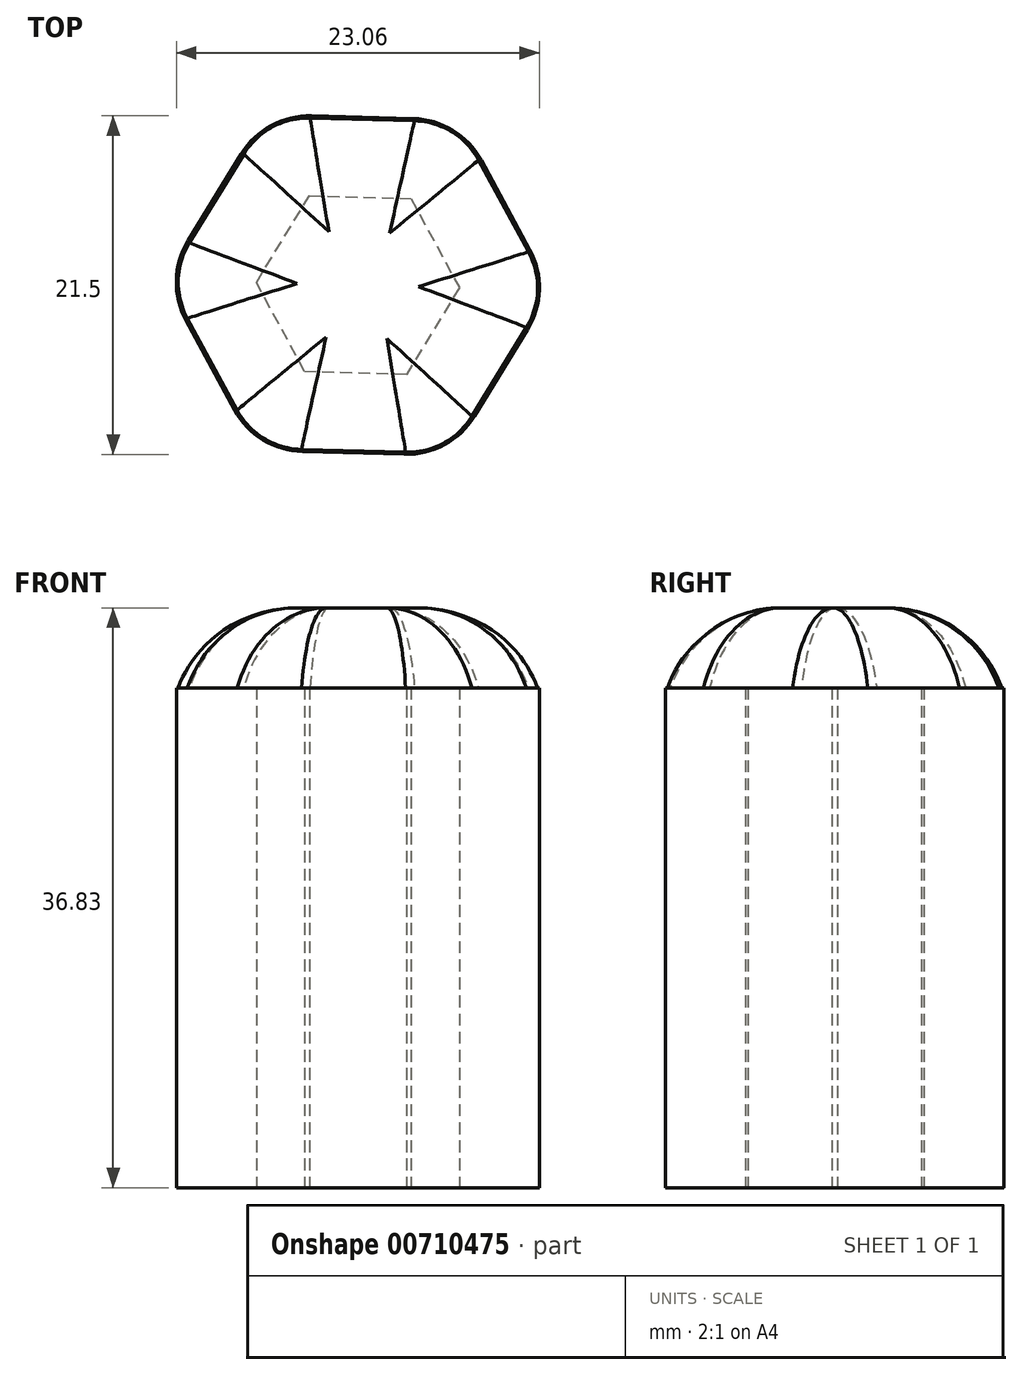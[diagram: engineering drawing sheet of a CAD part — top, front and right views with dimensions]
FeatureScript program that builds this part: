
annotation { "Feature Type Name" : "Feature", "Feature Type Description" : "" }
export const myFeature = defineFeature(function(context is Context, id is Id, definition is map)
    precondition{}
    {
        {
            var Q0;
            Q0=qCreatedBy(makeId("Top.planeOp"),FACE);
            var sketch = newSketch(context, id + "F0", { "sketchPlane" : qUnion([Q0])});
            skCircle(sketch, "E0.cCircle", {"center": v(0, 0) * mm, "radius": 5.59 * mm, "construction": true});
            skLineSegment(sketch, "E0.0", {"start": v(6.45, -0.17) * mm, "end": v(3.08, -5.67) * mm});
            skLineSegment(sketch, "E0.1", {"start": v(3.08, -5.67) * mm, "end": v(-3.37, -5.5) * mm});
            skLineSegment(sketch, "E0.2", {"start": v(-3.37, -5.5) * mm, "end": v(-6.45, 0.17) * mm});
            skLineSegment(sketch, "E0.3", {"start": v(-6.45, 0.17) * mm, "end": v(-3.08, 5.67) * mm});
            skLineSegment(sketch, "E0.4", {"start": v(-3.08, 5.67) * mm, "end": v(3.37, 5.5) * mm});
            skLineSegment(sketch, "E0.5", {"start": v(3.37, 5.5) * mm, "end": v(6.45, -0.17) * mm});
            skPoint(sketch, "E0.0.midPoint", {"position": v(4.76, -2.92) * mm});
            skCircle(sketch, "E1.cCircle", {"center": v(0, 0) * mm, "radius": 10.67 * mm, "construction": true});
            skLineSegment(sketch, "E1.0", {"start": v(12.31, -0.32) * mm, "end": v(5.88, -10.83) * mm});
            skLineSegment(sketch, "E1.1", {"start": v(5.88, -10.83) * mm, "end": v(-6.44, -10.5) * mm});
            skLineSegment(sketch, "E1.2", {"start": v(-6.44, -10.5) * mm, "end": v(-12.31, 0.32) * mm});
            skLineSegment(sketch, "E1.3", {"start": v(-12.31, 0.32) * mm, "end": v(-5.88, 10.83) * mm});
            skLineSegment(sketch, "E1.4", {"start": v(-5.88, 10.83) * mm, "end": v(6.44, 10.5) * mm});
            skLineSegment(sketch, "E1.5", {"start": v(6.44, 10.5) * mm, "end": v(12.31, -0.32) * mm});
            skPoint(sketch, "E1.0.midPoint", {"position": v(9.1, -5.57) * mm});
            skSolve(sketch);
        }
        {
            var Q0;
            Q0 = qSketchRegion(id + "F0", true);
            extrude(context, id + "F1", {"entities" : qUnion([Q0]), "depth" : 31.75 * mm, "offsetDistance" : 25.4 * mm});
        }
        {
            var Q0;
            Q0=makeQuery(id+"F1.opExtrude","CAP_FACE",FACE,{"disambiguationData":[OSD([sQuery(id+"F0.wireOp",EDGE,"E0.0"),sQuery(id+"F0.wireOp",EDGE,"E0.1"),sQuery(id+"F0.wireOp",EDGE,"E0.2"),sQuery(id+"F0.wireOp",EDGE,"E0.3"),sQuery(id+"F0.wireOp",EDGE,"E0.4"),sQuery(id+"F0.wireOp",EDGE,"E0.5"),sQuery(id+"F0.wireOp",EDGE,"E1.0"),sQuery(id+"F0.wireOp",EDGE,"E1.1"),sQuery(id+"F0.wireOp",EDGE,"E1.2"),sQuery(id+"F0.wireOp",EDGE,"E1.3"),sQuery(id+"F0.wireOp",EDGE,"E1.4"),sQuery(id+"F0.wireOp",EDGE,"E1.5")])],"isStart":false});
            var sketch = newSketch(context, id + "F2", { "sketchPlane" : qUnion([Q0])});
            skCircle(sketch, "E2.cCircle", {"center": v(0, 0) * mm, "radius": 10.53 * mm, "construction": true});
            skLineSegment(sketch, "E2.0", {"start": v(12.15, -0.32) * mm, "end": v(5.8, -10.68) * mm});
            skLineSegment(sketch, "E2.1", {"start": v(5.8, -10.68) * mm, "end": v(-6.35, -10.36) * mm});
            skLineSegment(sketch, "E2.2", {"start": v(-6.35, -10.36) * mm, "end": v(-12.15, 0.32) * mm});
            skLineSegment(sketch, "E2.3", {"start": v(-12.15, 0.32) * mm, "end": v(-5.8, 10.68) * mm});
            skLineSegment(sketch, "E2.4", {"start": v(-5.8, 10.68) * mm, "end": v(6.35, 10.36) * mm});
            skLineSegment(sketch, "E2.5", {"start": v(6.35, 10.36) * mm, "end": v(12.15, -0.32) * mm});
            skPoint(sketch, "E2.0.midPoint", {"position": v(8.98, -5.5) * mm});
            skSolve(sketch);
        }
        {
            var Q0;
            Q0 = qSketchRegion(id + "F2", true);
            extrude(context, id + "F3", {"entities" : qUnion([Q0]), "operationType" : NewBodyOperationType.ADD, "depth" : 5.08 * mm, "offsetDistance" : 25.4 * mm});
        }
        {
            var Q0;
            Q0=makeQuery(id+"F3.opExtrude","CAP_EDGE",EDGE,{"disambiguationData":[OSD([sQuery(id+"F2.wireOp",EDGE,"E2.1")])],"isStart":false});
            var Q1;
            Q1=makeQuery(id+"F3.opExtrude","CAP_EDGE",EDGE,{"disambiguationData":[OSD([sQuery(id+"F2.wireOp",EDGE,"E2.0")])],"isStart":false});
            var Q2;
            Q2=makeQuery(id+"F3.opExtrude","CAP_EDGE",EDGE,{"disambiguationData":[OSD([sQuery(id+"F2.wireOp",EDGE,"E2.2")])],"isStart":false});
            var Q3;
            Q3=makeQuery(id+"F3.opExtrude","CAP_EDGE",EDGE,{"disambiguationData":[OSD([sQuery(id+"F2.wireOp",EDGE,"E2.3")])],"isStart":false});
            var Q4;
            Q4=makeQuery(id+"F3.opExtrude","CAP_EDGE",EDGE,{"disambiguationData":[OSD([sQuery(id+"F2.wireOp",EDGE,"E2.4")])],"isStart":false});
            var Q5;
            Q5=makeQuery(id+"F3.opExtrude","CAP_EDGE",EDGE,{"disambiguationData":[OSD([sQuery(id+"F2.wireOp",EDGE,"E2.5")])],"isStart":false});
            fillet(context, id + "F4", {"entities" : qUnion([Q0, Q1, Q2, Q3, Q4, Q5]), "radius" : 7.62 * mm, "tangentPropagation" : true, "allowEdgeOverflow" : false});
        }
        {
            var Q0;
            Q0=makeQuery(id+"F4.opFillet","BLEND_EDGE",EDGE,{"blendedFrom":[makeQuery(id+"F3.opExtrude","CAP_EDGE",EDGE,{"disambiguationData":[OSD([sQuery(id+"F2.wireOp",EDGE,"E2.0")])],"isStart":false}),makeQuery(id+"F3.opExtrude","CAP_EDGE",EDGE,{"disambiguationData":[OSD([sQuery(id+"F2.wireOp",EDGE,"E2.5")])],"isStart":false})],"blendedInto":[]});
            var Q1;
            Q1=makeQuery(id+"F1.opExtrude","SWEPT_EDGE",EDGE,{"disambiguationData":[OSD([sQuery(id+"F0.wireOp",EDGE,"E1.4"),sQuery(id+"F0.wireOp",EDGE,"E1.5")])]});
            var Q2;
            Q2=makeQuery(id+"F1.opExtrude","SWEPT_EDGE",EDGE,{"disambiguationData":[OSD([sQuery(id+"F0.wireOp",EDGE,"E1.0"),sQuery(id+"F0.wireOp",EDGE,"E1.5")])]});
            var Q3;
            Q3=makeQuery(id+"F4.opFillet","BLEND_EDGE",EDGE,{"blendedFrom":[makeQuery(id+"F3.opExtrude","CAP_EDGE",EDGE,{"disambiguationData":[OSD([sQuery(id+"F2.wireOp",EDGE,"E2.4")])],"isStart":false}),makeQuery(id+"F3.opExtrude","CAP_EDGE",EDGE,{"disambiguationData":[OSD([sQuery(id+"F2.wireOp",EDGE,"E2.5")])],"isStart":false})],"blendedInto":[]});
            var Q4;
            Q4=makeQuery(id+"F4.opFillet","BLEND_EDGE",EDGE,{"blendedFrom":[makeQuery(id+"F3.opExtrude","CAP_EDGE",EDGE,{"disambiguationData":[OSD([sQuery(id+"F2.wireOp",EDGE,"E2.3")])],"isStart":false}),makeQuery(id+"F3.opExtrude","CAP_EDGE",EDGE,{"disambiguationData":[OSD([sQuery(id+"F2.wireOp",EDGE,"E2.4")])],"isStart":false})],"blendedInto":[]});
            var Q5;
            Q5=makeQuery(id+"F4.opFillet","BLEND_EDGE",EDGE,{"blendedFrom":[makeQuery(id+"F3.opExtrude","CAP_EDGE",EDGE,{"disambiguationData":[OSD([sQuery(id+"F2.wireOp",EDGE,"E2.0")])],"isStart":false}),makeQuery(id+"F3.opExtrude","CAP_EDGE",EDGE,{"disambiguationData":[OSD([sQuery(id+"F2.wireOp",EDGE,"E2.1")])],"isStart":false})],"blendedInto":[]});
            var Q6;
            Q6=makeQuery(id+"F4.opFillet","BLEND_EDGE",EDGE,{"blendedFrom":[makeQuery(id+"F3.opExtrude","CAP_EDGE",EDGE,{"disambiguationData":[OSD([sQuery(id+"F2.wireOp",EDGE,"E2.1")])],"isStart":false}),makeQuery(id+"F3.opExtrude","CAP_EDGE",EDGE,{"disambiguationData":[OSD([sQuery(id+"F2.wireOp",EDGE,"E2.2")])],"isStart":false})],"blendedInto":[]});
            var Q7;
            Q7=makeQuery(id+"F4.opFillet","BLEND_EDGE",EDGE,{"blendedFrom":[makeQuery(id+"F3.opExtrude","CAP_EDGE",EDGE,{"disambiguationData":[OSD([sQuery(id+"F2.wireOp",EDGE,"E2.2")])],"isStart":false}),makeQuery(id+"F3.opExtrude","CAP_EDGE",EDGE,{"disambiguationData":[OSD([sQuery(id+"F2.wireOp",EDGE,"E2.3")])],"isStart":false})],"blendedInto":[]});
            var Q8;
            Q8=makeQuery(id+"F1.opExtrude","SWEPT_EDGE",EDGE,{"disambiguationData":[OSD([sQuery(id+"F0.wireOp",EDGE,"E1.0"),sQuery(id+"F0.wireOp",EDGE,"E1.1")])]});
            var Q9;
            Q9=makeQuery(id+"F1.opExtrude","SWEPT_EDGE",EDGE,{"disambiguationData":[OSD([sQuery(id+"F0.wireOp",EDGE,"E1.1"),sQuery(id+"F0.wireOp",EDGE,"E1.2")])]});
            var Q10;
            Q10=makeQuery(id+"F1.opExtrude","SWEPT_EDGE",EDGE,{"disambiguationData":[OSD([sQuery(id+"F0.wireOp",EDGE,"E1.2"),sQuery(id+"F0.wireOp",EDGE,"E1.3")])]});
            var Q11;
            Q11=makeQuery(id+"F1.opExtrude","SWEPT_EDGE",EDGE,{"disambiguationData":[OSD([sQuery(id+"F0.wireOp",EDGE,"E1.3"),sQuery(id+"F0.wireOp",EDGE,"E1.4")])]});
            fillet(context, id + "F5", {"entities" : qUnion([Q0, Q1, Q2, Q3, Q4, Q5, Q6, Q7, Q8, Q9, Q10, Q11]), "radius" : 5.08 * mm, "tangentPropagation" : true, "allowEdgeOverflow" : false});
        }
    });
